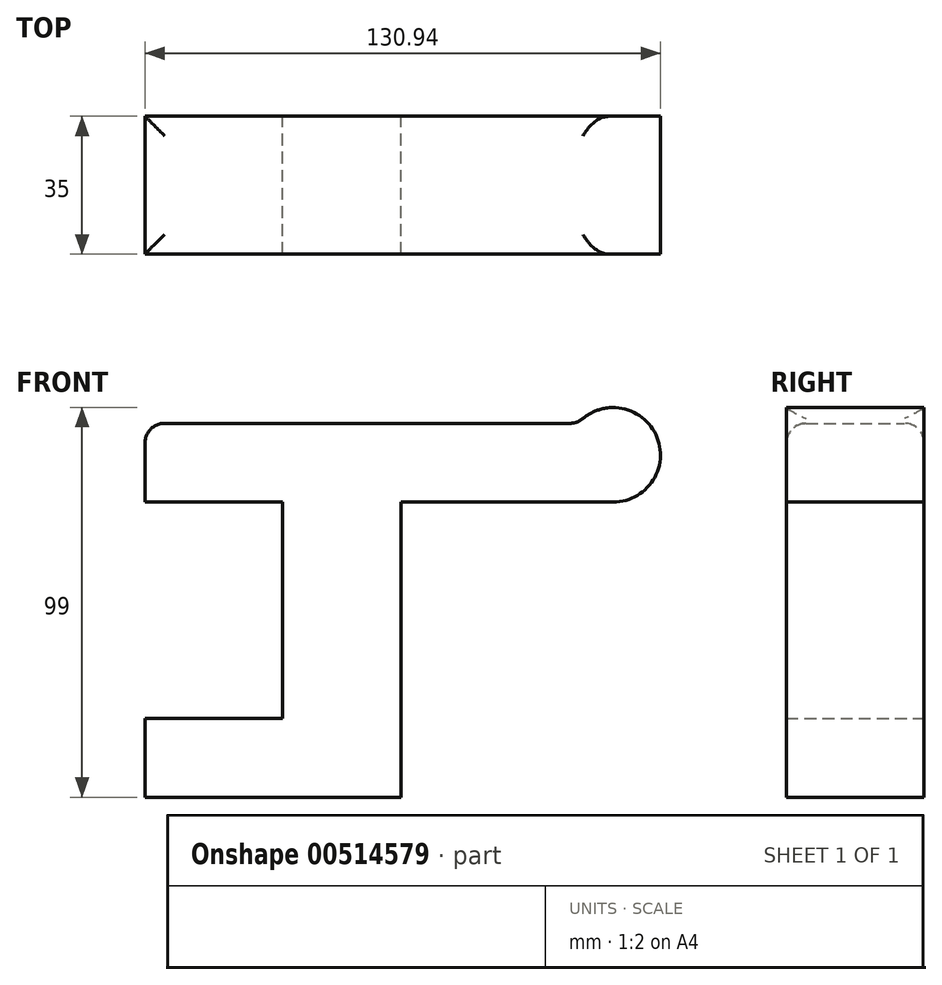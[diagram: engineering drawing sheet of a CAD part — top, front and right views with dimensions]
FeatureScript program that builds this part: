
annotation { "Feature Type Name" : "Feature", "Feature Type Description" : "" }
export const myFeature = defineFeature(function(context is Context, id is Id, definition is map)
    precondition{}
    {
        {
            var Q0;
            Q0=qCreatedBy(makeId("Front.planeOp"),FACE);
            var sketch = newSketch(context, id + "F0", { "sketchPlane" : qUnion([Q0])});
            skLineSegment(sketch, "E0", {"start": v(0, 0) * mm, "end": v(0, 20) * mm});
            skLineSegment(sketch, "E1", {"start": v(0, 20) * mm, "end": v(35, 20) * mm});
            skLineSegment(sketch, "E2", {"start": v(35, 20) * mm, "end": v(35, 75) * mm});
            skLineSegment(sketch, "E3", {"start": v(35, 75) * mm, "end": v(0, 75) * mm});
            skLineSegment(sketch, "E4", {"start": v(0, 75) * mm, "end": v(0, 95) * mm});
            skLineSegment(sketch, "E5", {"start": v(0, 95) * mm, "end": v(110, 95) * mm});
            skLineSegment(sketch, "E6", {"start": v(118.94, 75) * mm, "end": v(65, 75) * mm});
            skLineSegment(sketch, "E7", {"start": v(65, 75) * mm, "end": v(65, 0) * mm});
            skLineSegment(sketch, "E8", {"start": v(65, 0) * mm, "end": v(0, 0) * mm});
            skArc(sketch, "E9", {"start": v(118.94, 75) * mm, "mid": v(129.9, 91.9) * mm, "end": v(110, 95) * mm});
            skSolve(sketch);
        }
        {
            var Q0;
            Q0=makeQuery(id+"F0.imprint","IMPRINT",FACE,{"disambiguationData":[TD([[makeQuery(id+"F0.imprint","IMPRINT",EDGE,{"derivedFrom":sQuery(id+"F0.wireOp",EDGE,"E0")}),-1.0]])]});
            extrude(context, id + "F1", {"entities" : qUnion([Q0]), "depth" : 35 * mm, "offsetDistance" : 25 * mm});
        }
        {
            var Q0;
            Q0=makeQuery(id+"F1.opExtrude","SWEPT_FACE",FACE,{"disambiguationData":[OSD([sQuery(id+"F0.wireOp",EDGE,"E5")])]});
            fillet(context, id + "F2", {"entities" : qUnion([Q0]), "radius" : 5 * mm, "tangentPropagation" : true, "allowEdgeOverflow" : false});
        }
    });
